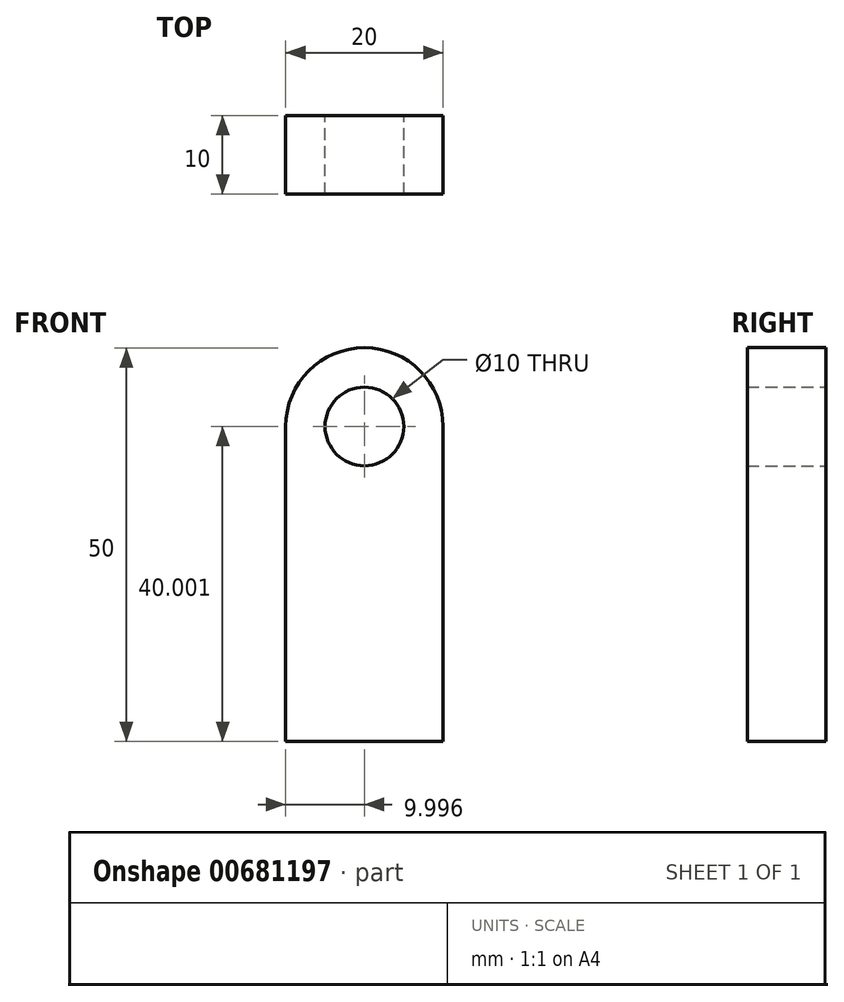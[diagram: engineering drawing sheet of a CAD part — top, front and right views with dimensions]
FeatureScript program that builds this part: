
annotation { "Feature Type Name" : "Feature", "Feature Type Description" : "" }
export const myFeature = defineFeature(function(context is Context, id is Id, definition is map)
    precondition{}
    {
        {
            var Q0;
            Q0=qCreatedBy(makeId("Front.planeOp"),FACE);
            var sketch = newSketch(context, id + "F0", { "sketchPlane" : qUnion([Q0])});
            skLineSegment(sketch, "E0.top", {"start": v(-10.01, -31.76) * mm, "end": v(9.99, -31.76) * mm});
            skLineSegment(sketch, "E0.left", {"start": v(-10.01, 8.24) * mm, "end": v(-10.01, -31.76) * mm});
            skLineSegment(sketch, "E0.right", {"start": v(9.99, 8.24) * mm, "end": v(9.99, -31.76) * mm});
            skArc(sketch, "E1", {"start": v(9.99, 8.24) * mm, "mid": v(-0.01, 18.24) * mm, "end": v(-10.01, 8.24) * mm});
            skCircle(sketch, "E2", {"center": v(-0.01, 8.24) * mm, "radius": 5 * mm});
            skSolve(sketch);
        }
        {
            var Q0;
            Q0=makeQuery(id+"F0.imprint","IMPRINT",FACE,{"disambiguationData":[TD([[makeQuery(id+"F0.imprint","IMPRINT",EDGE,{"derivedFrom":sQuery(id+"F0.wireOp",EDGE,"E0.top")}),1.0]])]});
            extrude(context, id + "F1", {"entities" : qUnion([Q0]), "depth" : 10 * mm, "offsetDistance" : 25 * mm});
        }
    });
